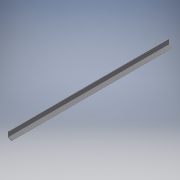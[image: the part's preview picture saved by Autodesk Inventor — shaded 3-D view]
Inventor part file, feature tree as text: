
AUTODESK INVENTOR PART (.ipt)
format: ipt  version: 2018 (Build 220112000, 112)  size: 99,328 bytes
history: native  units: mm
features: other x1, extrude x1, sketch x1
ambient origin geometry x8: Origin, YZ Plane, XZ Plane, XY Plane, X Axis, Y Axis, Z Axis, Center Point
bodies: Body1 (feature_tree)
feature tree (3):
  other  "ソリッド1"
  extrude  "押し出し1"  Depth=7.0mm
  sketch  "スケッチ1"
